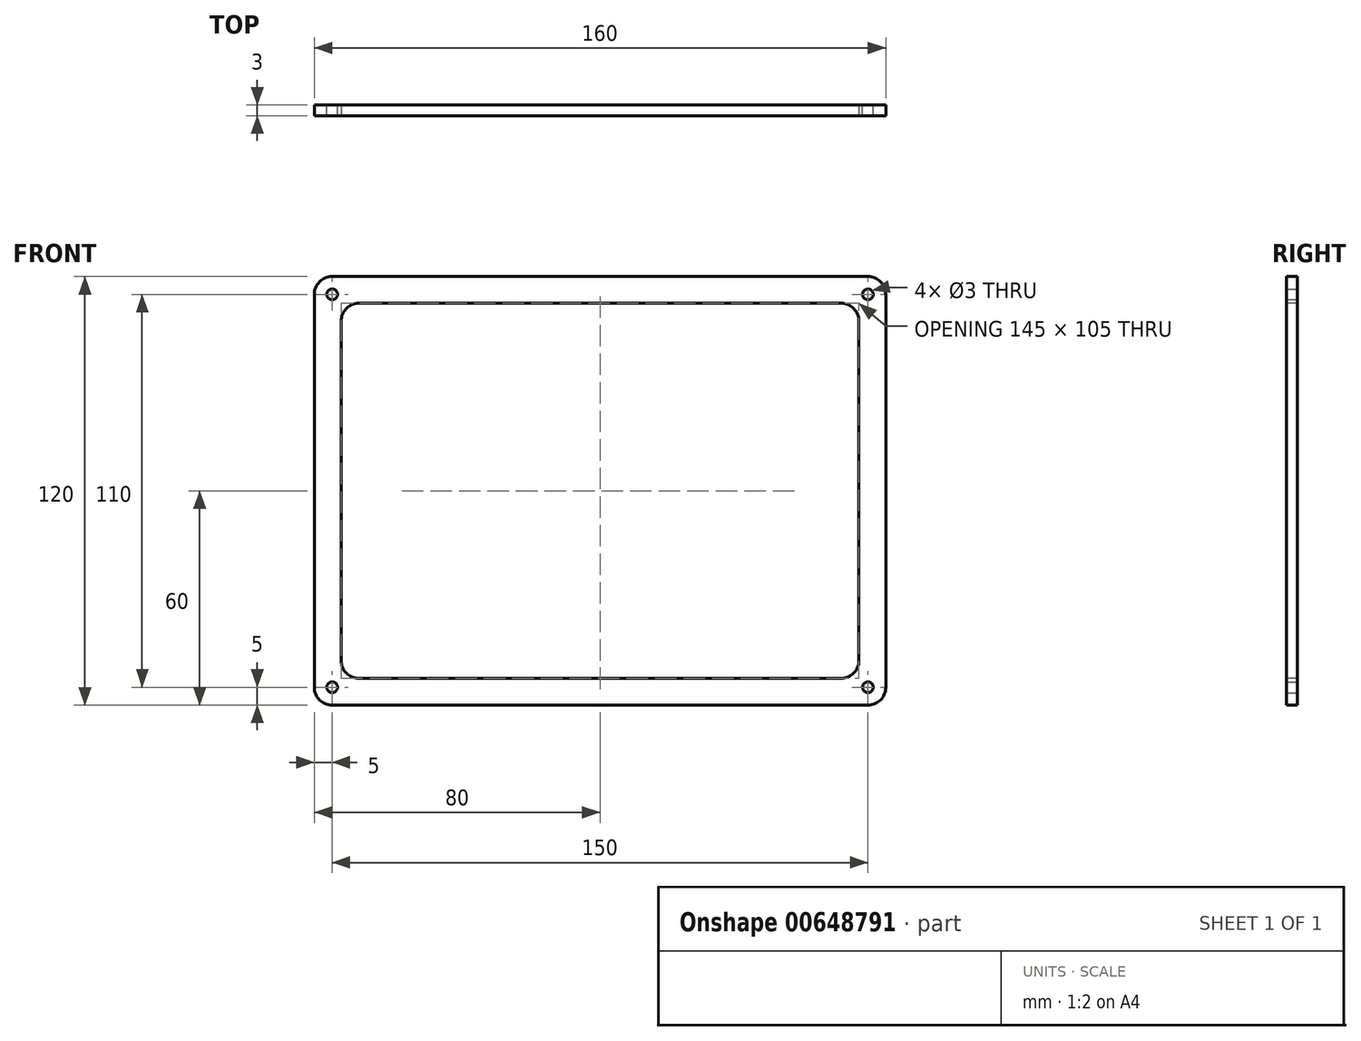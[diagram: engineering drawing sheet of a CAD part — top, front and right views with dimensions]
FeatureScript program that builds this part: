
annotation { "Feature Type Name" : "Feature", "Feature Type Description" : "" }
export const myFeature = defineFeature(function(context is Context, id is Id, definition is map)
    precondition{}
    {
        {
            var Q0;
            Q0=qCreatedBy(makeId("Front.planeOp"),FACE);
            var sketch = newSketch(context, id + "F0", { "sketchPlane" : qUnion([Q0])});
            skLineSegment(sketch, "E0.bottom", {"start": v(75, -60) * mm, "end": v(-75, -60) * mm});
            skLineSegment(sketch, "E0.top", {"start": v(75, 60) * mm, "end": v(-75, 60) * mm});
            skLineSegment(sketch, "E0.left", {"start": v(80, -55) * mm, "end": v(80, 55) * mm});
            skLineSegment(sketch, "E0.right", {"start": v(-80, -55) * mm, "end": v(-80, 55) * mm});
            skPoint(sketch, "E0.middle", {"position": v(0, 0) * mm});
            skPoint(sketch, "E1.visualSharp", {"position": v(-80, 60) * mm});
            skArc(sketch, "E1.filletArc", {"start": v(-75, 60) * mm, "mid": v(-78.54, 58.54) * mm, "end": v(-80, 55) * mm});
            skPoint(sketch, "E2.visualSharp", {"position": v(80, 60) * mm});
            skArc(sketch, "E2.filletArc", {"start": v(80, 55) * mm, "mid": v(78.54, 58.54) * mm, "end": v(75, 60) * mm});
            skPoint(sketch, "E3.visualSharp", {"position": v(80, -60) * mm});
            skArc(sketch, "E3.filletArc", {"start": v(75, -60) * mm, "mid": v(78.54, -58.54) * mm, "end": v(80, -55) * mm});
            skPoint(sketch, "E4.visualSharp", {"position": v(-80, -60) * mm});
            skArc(sketch, "E4.filletArc", {"start": v(-80, -55) * mm, "mid": v(-78.54, -58.54) * mm, "end": v(-75, -60) * mm});
            skSolve(sketch);
        }
        {
            var Q0;
            Q0=makeQuery(id+"F0.imprint","IMPRINT",FACE,{"disambiguationData":[TD([[makeQuery(id+"F0.imprint","IMPRINT",EDGE,{"derivedFrom":sQuery(id+"F0.wireOp",EDGE,"E0.bottom")}),-1.0]])]});
            extrude(context, id + "F1", {"entities" : qUnion([Q0]), "depth" : 3 * mm, "offsetDistance" : 25 * mm});
        }
        {
            var Q0;
            Q0=qCreatedBy(makeId("Front.planeOp"),FACE);
            var sketch = newSketch(context, id + "F2", { "sketchPlane" : qUnion([Q0])});
            skCircle(sketch, "E5", {"center": v(-75, 55) * mm, "radius": 1.5 * mm});
            skCircle(sketch, "E6", {"center": v(75, 55) * mm, "radius": 1.5 * mm});
            skCircle(sketch, "E7", {"center": v(75, -55) * mm, "radius": 1.5 * mm});
            skCircle(sketch, "E8", {"center": v(-75, -55) * mm, "radius": 1.5 * mm});
            skSolve(sketch);
        }
        {
            var Q0;
            Q0=qSketchRegion(id+"F2",true);
            extrude(context, id + "F3", {"entities" : qUnion([Q0]), "operationType" : NewBodyOperationType.REMOVE, "depth" : 25 * mm, "offsetDistance" : 25 * mm});
        }
        {
            var Q0;
            Q0=makeQuery(id+"F1.opExtrude","CAP_FACE",FACE,{"disambiguationData":[OSD([sQuery(id+"F0.wireOp",EDGE,"E0.bottom"),sQuery(id+"F0.wireOp",EDGE,"E0.top"),sQuery(id+"F0.wireOp",EDGE,"E0.left"),sQuery(id+"F0.wireOp",EDGE,"E0.right"),sQuery(id+"F0.wireOp",EDGE,"E1.filletArc"),sQuery(id+"F0.wireOp",EDGE,"E2.filletArc"),sQuery(id+"F0.wireOp",EDGE,"E3.filletArc"),sQuery(id+"F0.wireOp",EDGE,"E4.filletArc")])],"isStart":false});
            var sketch = newSketch(context, id + "F4", { "sketchPlane" : qUnion([Q0])});
            skLineSegment(sketch, "E9.bottom", {"start": v(67.5, 52.5) * mm, "end": v(-67.5, 52.5) * mm});
            skLineSegment(sketch, "E9.top", {"start": v(67.5, -52.5) * mm, "end": v(-67.5, -52.5) * mm});
            skLineSegment(sketch, "E9.left", {"start": v(72.5, 47.5) * mm, "end": v(72.5, -47.5) * mm});
            skLineSegment(sketch, "E9.right", {"start": v(-72.5, 47.5) * mm, "end": v(-72.5, -47.5) * mm});
            skPoint(sketch, "E9.middle", {"position": v(0, 0) * mm});
            skPoint(sketch, "E10.visualSharp", {"position": v(-72.5, 52.5) * mm});
            skArc(sketch, "E10.filletArc", {"start": v(-67.5, 52.5) * mm, "mid": v(-71.04, 51.04) * mm, "end": v(-72.5, 47.5) * mm});
            skPoint(sketch, "E11.visualSharp", {"position": v(72.5, 52.5) * mm});
            skArc(sketch, "E11.filletArc", {"start": v(72.5, 47.5) * mm, "mid": v(71.04, 51.04) * mm, "end": v(67.5, 52.5) * mm});
            skPoint(sketch, "E12.visualSharp", {"position": v(72.5, -52.5) * mm});
            skArc(sketch, "E12.filletArc", {"start": v(67.5, -52.5) * mm, "mid": v(71.04, -51.04) * mm, "end": v(72.5, -47.5) * mm});
            skPoint(sketch, "E13.visualSharp", {"position": v(-72.5, -52.5) * mm});
            skArc(sketch, "E13.filletArc", {"start": v(-72.5, -47.5) * mm, "mid": v(-71.04, -51.04) * mm, "end": v(-67.5, -52.5) * mm});
            skSolve(sketch);
        }
        {
            var Q0;
            Q0 = qSketchRegion(id + "F4", true);
            extrude(context, id + "F5", {"entities" : qUnion([Q0]), "operationType" : NewBodyOperationType.REMOVE, "oppositeDirection" : true, "depth" : 3 * mm, "offsetDistance" : 25 * mm});
        }
    });
